# Revit family: Shower Seat_Metlam_Folding_Support Legs and Handle
name_source: partatom
category: Specialty Equipment
revit_build: Autodesk Revit 2016 (Build: 20170117_1200(x64)
units: mm (PartAtom-declared; Revit-internal decimal feet)

## family parameters
Always vertical = Yes
Cut with Voids When Loaded = No
OmniClass Number = 23.45.05.14.11.17
OmniClass Title = Shower/Bath Seats
Part Type = Normal
Room Calculation Point = Yes
Round Connector Dimension = Use Diameter
Shared = No
Work Plane-Based = No

## types (1)
- 960w x 400d x 480h (ML995_PH)
    Description = Phenolic Compound Folding Shower Seat with Handle
    Frame_Material = z_Metlam_Metal_Stainless Steel_Satin
    Manufacturer = Metlam
    Manufacturer_Overall Depth = 400 mm  [stored 1.31234 ft]
    Manufacturer_Overall Height = 480 mm  [stored 1.5748 ft]
    Manufacturer_Overall Width = 960 mm
    Manufacturer_Spec Code = ML995_PH
    Manufacturer_URL__Product Specific = https://www.metlam.com.au
    Material_ANZRS = z_Metlam_White
    Model = ML995_PH
    Seat Edge_Material = z_Metlam_Black
    Type Comments = Shower Seats
    URL = http://www.metlam.com.au

note: [stored X ft] marks values corroborated as IEEE doubles in the binary element streams (Revit-internal decimal feet)

## geometry (parser evidence)
native form markers: Sweep x2
no freeform markers — native parametric forms only
